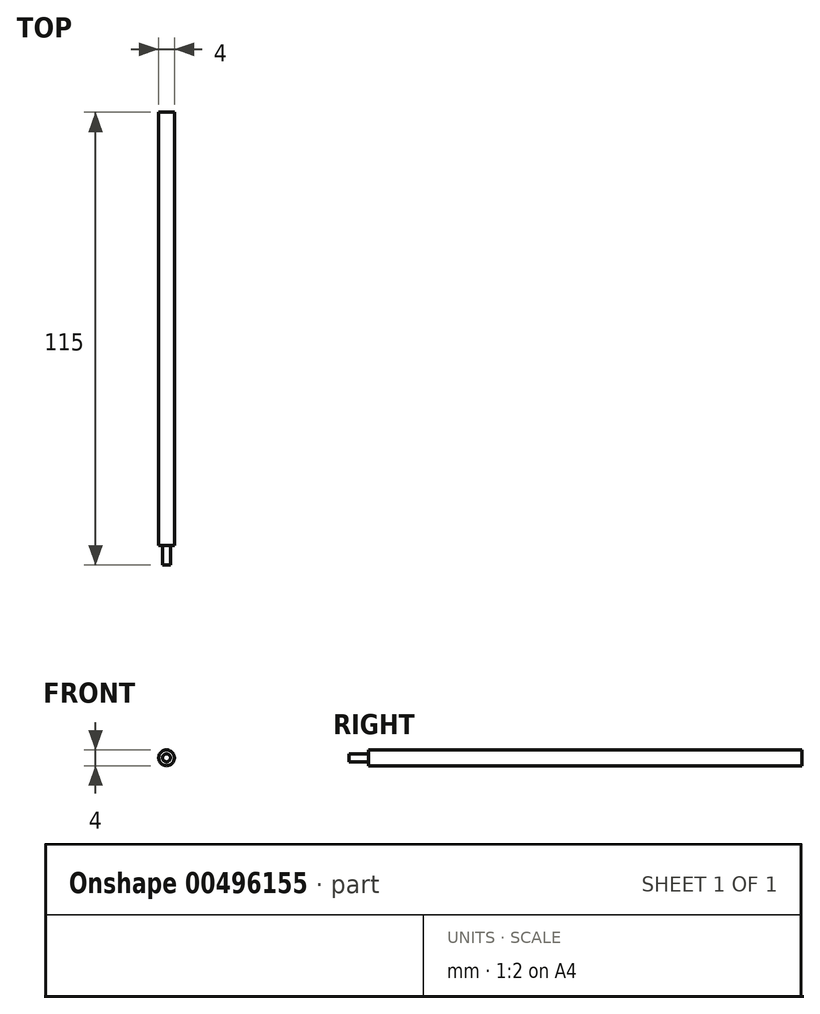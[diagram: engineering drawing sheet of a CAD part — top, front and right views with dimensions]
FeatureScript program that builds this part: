
annotation { "Feature Type Name" : "Feature", "Feature Type Description" : "" }
export const myFeature = defineFeature(function(context is Context, id is Id, definition is map)
    precondition{}
    {
        {
            var Q0;
            Q0=qCreatedBy(makeId("Front.planeOp"),FACE);
            var sketch = newSketch(context, id + "F0", { "sketchPlane" : qUnion([Q0])});
            skCircle(sketch, "E0", {"center": v(0, 0) * mm, "radius": 2 * mm});
            skSolve(sketch);
        }
        {
            var Q0;
            Q0=qSketchRegion(id+"F0",true);
            extrude(context, id + "F1", {"entities" : qUnion([Q0]), "oppositeDirection" : true, "depth" : 110 * mm, "offsetDistance" : 25 * mm});
        }
        {
            var Q0;
            Q0=makeQuery(id+"F1.opExtrude","CAP_FACE",FACE,{"disambiguationData":[OSD([sQuery(id+"F0.wireOp",EDGE,"E0")])],"isStart":true});
            var sketch = newSketch(context, id + "F2", { "sketchPlane" : qUnion([Q0])});
            skCircle(sketch, "E1", {"center": v(0, 0) * mm, "radius": 1 * mm});
            skSolve(sketch);
        }
        {
            var Q0;
            Q0=qSketchRegion(id+"F2",true);
            extrude(context, id + "F3", {"entities" : qUnion([Q0]), "operationType" : NewBodyOperationType.ADD, "depth" : 5 * mm});
        }
    });
